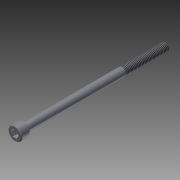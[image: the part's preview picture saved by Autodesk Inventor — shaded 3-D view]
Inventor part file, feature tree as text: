
AUTODESK INVENTOR PART (.ipt)
format: ipt  version: 2011 (Build 150239000, 239)  size: 93,696 bytes
history: native  units: in
note: dims shown in document units (in); Inventor stores cm internally (conversion verified against a paired STEP export)
features: extrude x3, sketch x3, chamfer x2, thread x1
ambient origin geometry x8: Origin, YZ Plane, XZ Plane, XY Plane, X Axis, Y Axis, Z Axis, Center Point
bodies: Solid1 (feature_tree)
feature tree (9):
  extrude  "Extrusion1"  Depth=0.19in TaperAngle=0.0deg
  extrude  "Extrusion2"  Depth=3.25in TaperAngle=0.0deg
  extrude  "Extrusion3"  Depth=0.125in TaperAngle=0.0deg
  thread  "Thread1"  [1 undecoded]
  chamfer  "Chamfer1"  Distance=0.02in Angle=45.0deg
  chamfer  "Chamfer2"  Distance=0.02in Angle=45.0deg
  sketch  "Sketch1"  dims[d0=0.312in d1=0.19in d2=0.0in]
  sketch  "Sketch2"  dims[d3=0.19in d4=3.25in d5=0.0in]
  sketch  "Sketch3"  dims[d6=0.1562in d7=0.125in d8=0.0in d9=1.0in d10=0.0in d11=0.02in d12=0.125in d13=45.0deg d14=0.02in d15=0.125in d16=45.0deg]
note: 1 required parameter value undecoded (feature->parameter linkage not recoverable at this tier; creation-order binding heuristic only, values carry confidence <= 0.55)
